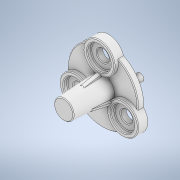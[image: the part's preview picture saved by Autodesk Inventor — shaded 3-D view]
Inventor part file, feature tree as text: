
AUTODESK INVENTOR PART (.ipt)
format: ipt  version: 2021 (Build 250183000, 183)  size: 337,408 bytes
history: native  units: mm
features: sketch x9, extrude x7, pattern_circular x4, fillet x2, other x1, revolve x1
ambient origin geometry x8: Origin, YZ Plane, XZ Plane, XY Plane, X Axis, Y Axis, Z Axis, Center Point
bodies: Body1 (feature_tree)
feature tree (24):
  other  "ソリッド1"
  extrude  "押し出し1"  Depth=18.0mm
  extrude  "押し出し2"  Depth=1.5mm TaperAngle=0.0deg
  pattern_circular  "円形状パターン1"  [2 undecoded]
  extrude  "押し出し3"  Depth=7.0mm
  extrude  "押し出し4"  Depth=2.5mm TaperAngle=0.0deg
  pattern_circular  "円形状パターン2"  Count=3 Angle=360.0deg
  sketch  "スケッチ5"
  revolve  "回転1"
  extrude  "押し出し5"  Depth=3.0mm
  pattern_circular  "円形状パターン3"  [2 undecoded]
  extrude  "押し出し6"  Depth=6.0mm
  pattern_circular  "円形状パターン4"  [2 undecoded]
  fillet  "フィレット1"  Radius=30.0mm
  fillet  "フィレット2"  Radius=6.0mm
  extrude  "押し出し7"  Depth=3.0mm
  sketch  "スケッチ1"
  sketch  "スケッチ2"
  sketch  "スケッチ3"
  sketch  "スケッチ4"
  sketch  "スケッチ6"
  sketch  "スケッチ7"
  sketch  "スケッチ8"
  sketch  "スケッチ9"
note: 6 required parameter values undecoded (feature->parameter linkage not recoverable at this tier; creation-order binding heuristic only, values carry confidence <= 0.55)
